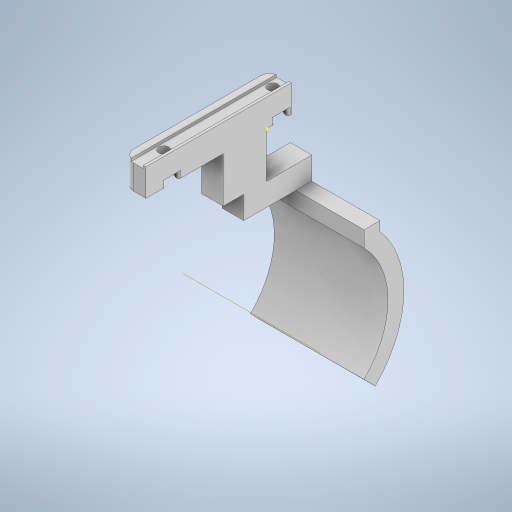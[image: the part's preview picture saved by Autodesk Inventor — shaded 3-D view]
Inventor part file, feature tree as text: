
AUTODESK INVENTOR PART (.ipt)
format: ipt  version: 2024 (Build 280153000, 153)  size: 390,656 bytes
history: native  units: in
note: dims shown in document units (in); Inventor stores cm internally (conversion verified against a paired STEP export)
features: sketch x10, extrude x6, projected_geometry x4, fillet x2, sweep x1, other x1, revolve x1
ambient origin geometry x8: Origin, YZ Plane, XZ Plane, XY Plane, X Axis, Y Axis, Z Axis, Center Point
bodies: Solid1 (feature_tree)
feature tree (25):
  extrude  "Extrusion1"  Depth=2.5197in
  extrude  "Extrusion2"  Depth=1.8898in
  extrude  "Extrusion3"  Depth=0.4724in TaperAngle=0.0deg
  fillet  "Fillet1"  Radius=0.0433in
  fillet  "Fillet2"  Radius=0.2126in
  extrude  "Extrusion19"  Depth=0.4724in TaperAngle=0.0deg
  extrude  "Extrusion21"  Depth=0.1181in TaperAngle=0.0deg
  sketch  "Sketch41"  dims[d17=0.1772in d18=0.0394in]
  extrude  "Extrusion22"  Depth=0.0394in
  sweep  "Sweep3"
  other  "Work Axis1"
  revolve  "Revolution1"  [1 undecoded]
  sketch  "Sketch1"  dims[d1=0.374in d2=2.5197in]
  sketch  "Sketch2"  dims[d3=0.1772in d4=1.8898in]
  sketch  "Sketch3"  dims[d6=0.1457in d7=0.4724in d8=0.0in d9=0.0433in d10=0.2126in]
  projected_geometry  "Projected Loop2"
  projected_geometry  "Projected Loop3"
  projected_geometry  "Projected Loop4"
  projected_geometry  "Projected Loop5"
  sketch  "Sketch28"  dims[d11=0.0472in d12=0.4724in d13=0.0in]
  sketch  "Sketch40"  dims[d14=0.2953in d15=0.1181in d16=0.0in]
  sketch  "Sketch42"  dims[d19=0.1575in d76=0.4724in]
  sketch  "Sketch44"  dims[d107=0.102in d108=0.748in]
  sketch  "Sketch45"  dims[d109=0.7874in d110=0.0in]
  sketch  "Sketch46"  dims[d130=0.7874in d131=1.1811in d132=0.3937in d133=0.0in d134=1.1811in d135=0.2756in d137=1.9685in d138=0.2756in d139=0.0in d142=1.9685in d143=1.378in d144=0.0in d145=0.0in d146=90.0deg d42=0.0197in d43=0.0344in d44=0.0197in d45=0.0344in d46=0.0in d47=0.0in d48=0.0in d49=0.0in d50=0.0in d51=0.0in d52=0.0in d53=0.0in d55=0.0197in d56=0.0344in d57=0.0197in d58=0.0344in d60=0.0197in d61=0.0344in d62=0.0197in d63=0.0344in d72=0.0197in d73=0.0344in d74=0.0197in d75=0.0344in d140=0.0197in d141=0.0344in]
note: 1 required parameter value undecoded (feature->parameter linkage not recoverable at this tier; creation-order binding heuristic only, values carry confidence <= 0.55)
